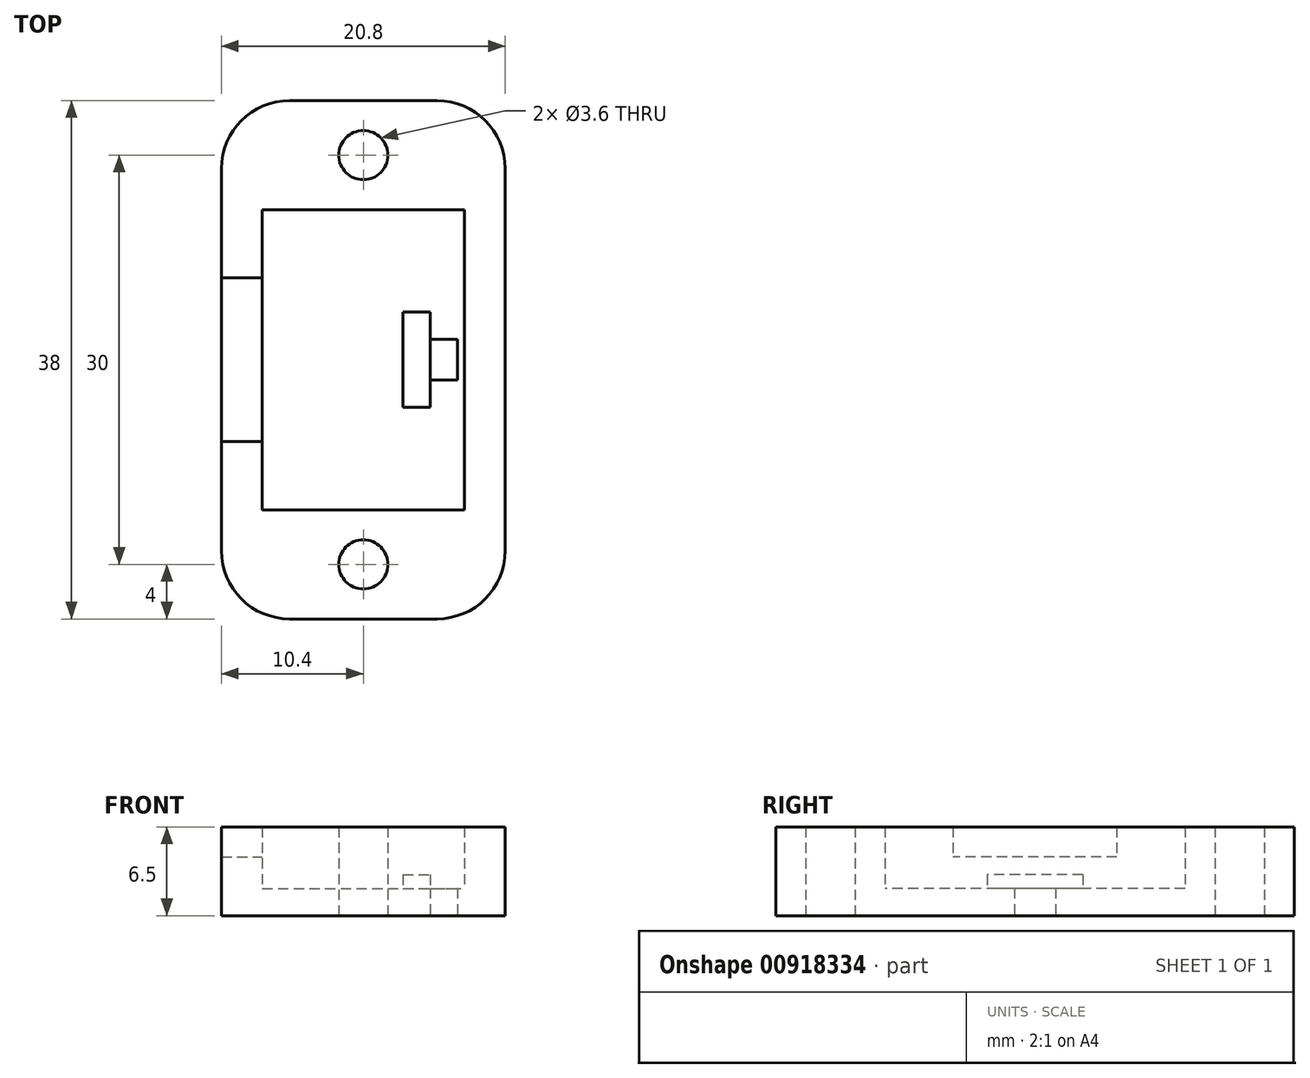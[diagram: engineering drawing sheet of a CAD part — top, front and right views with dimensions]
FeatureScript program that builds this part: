
annotation { "Feature Type Name" : "Feature", "Feature Type Description" : "" }
export const myFeature = defineFeature(function(context is Context, id is Id, definition is map)
    precondition{}
    {
        {
            var Q0;
            Q0=qCreatedBy(makeId("Top.planeOp"),FACE);
            var sketch = newSketch(context, id + "F0", { "sketchPlane" : qUnion([Q0])});
            skLineSegment(sketch, "E0.bottom", {"start": v(-7.4, 11) * mm, "end": v(7.4, 11) * mm});
            skLineSegment(sketch, "E0.top", {"start": v(-7.4, -11) * mm, "end": v(7.4, -11) * mm});
            skLineSegment(sketch, "E0.left", {"start": v(-7.4, 11) * mm, "end": v(-7.4, -11) * mm});
            skLineSegment(sketch, "E0.right", {"start": v(7.4, 11) * mm, "end": v(7.4, -11) * mm});
            skPoint(sketch, "E0.middle", {"position": v(0, 0) * mm});
            skLineSegment(sketch, "E1", {"start": v(2.9, 11) * mm, "end": v(2.9, -11) * mm, "construction": true});
            skLineSegment(sketch, "E2.bottom", {"start": v(2.9, 3.5) * mm, "end": v(4.9, 3.5) * mm});
            skLineSegment(sketch, "E2.top", {"start": v(2.9, -3.5) * mm, "end": v(4.9, -3.5) * mm});
            skLineSegment(sketch, "E2.left", {"start": v(2.9, 3.5) * mm, "end": v(2.9, -3.5) * mm});
            skLineSegment(sketch, "E2.right", {"start": v(4.9, 3.5) * mm, "end": v(4.9, -3.5) * mm});
            skPoint(sketch, "E2.middle", {"position": v(3.9, 0) * mm});
            skLineSegment(sketch, "E3.bottom", {"start": v(-10.4, 19) * mm, "end": v(10.4, 19) * mm});
            skLineSegment(sketch, "E3.top", {"start": v(-10.4, -19) * mm, "end": v(10.4, -19) * mm});
            skLineSegment(sketch, "E3.left", {"start": v(-10.4, 19) * mm, "end": v(-10.4, -19) * mm});
            skLineSegment(sketch, "E3.right", {"start": v(10.4, 19) * mm, "end": v(10.4, -19) * mm});
            skLineSegment(sketch, "E4.bottom", {"start": v(-10.4, 6) * mm, "end": v(-7.4, 6) * mm});
            skLineSegment(sketch, "E4.top", {"start": v(-10.4, -6) * mm, "end": v(-7.4, -6) * mm});
            skLineSegment(sketch, "E4.left", {"start": v(-10.4, 6) * mm, "end": v(-10.4, -6) * mm});
            skLineSegment(sketch, "E4.right", {"start": v(-7.4, 6) * mm, "end": v(-7.4, -6) * mm});
            skPoint(sketch, "E4.middle", {"position": v(-8.9, 0) * mm});
            skCircle(sketch, "E5", {"center": v(0, 15) * mm, "radius": 1.8 * mm});
            skCircle(sketch, "E6", {"center": v(0, -15) * mm, "radius": 1.8 * mm});
            skLineSegment(sketch, "E7.bottom", {"start": v(4.9, 1.5) * mm, "end": v(6.9, 1.5) * mm});
            skLineSegment(sketch, "E7.top", {"start": v(4.9, -1.5) * mm, "end": v(6.9, -1.5) * mm});
            skLineSegment(sketch, "E7.left", {"start": v(4.9, 1.5) * mm, "end": v(4.9, -1.5) * mm});
            skLineSegment(sketch, "E7.right", {"start": v(6.9, 1.5) * mm, "end": v(6.9, -1.5) * mm});
            skPoint(sketch, "E7.middle", {"position": v(5.9, 0) * mm});
            skSolve(sketch);
        }
        {
            var Q0;
            Q0=makeQuery(id+"F0.imprint","IMPRINT",FACE,{"disambiguationData":[TD([[makeQuery(id+"F0.imprint","IMPRINT",EDGE,{"derivedFrom":sQuery(id+"F0.wireOp",EDGE,"E0.bottom")}),1.0]])]});
            extrude(context, id + "F1", {"entities" : qUnion([Q0]), "depth" : 6.5 * mm, "offsetDistance" : 25 * mm});
        }
        {
            var Q0;
            Q0=makeQuery(id+"F0.imprint","IMPRINT",FACE,{"disambiguationData":[TD([[makeQuery(id+"F0.imprint","IMPRINT",EDGE,{"derivedFrom":sQuery(id+"F0.wireOp",EDGE,"E0.bottom")}),-1.0]])]});
            extrude(context, id + "F2", {"entities" : qUnion([Q0]), "operationType" : NewBodyOperationType.ADD, "depth" : 2 * mm, "offsetDistance" : 25 * mm});
        }
        {
            var Q0;
            Q0=makeQuery(id+"F0.imprint","IMPRINT",FACE,{"disambiguationData":[TD([[makeQuery(id+"F0.imprint","IMPRINT",EDGE,{"derivedFrom":sQuery(id+"F0.wireOp",EDGE,"E2.bottom")}),-1.0]])]});
            extrude(context, id + "F3", {"entities" : qUnion([Q0]), "operationType" : NewBodyOperationType.ADD, "depth" : 3 * mm, "offsetDistance" : 25 * mm});
        }
        {
            var Q0;
            Q0=makeQuery(id+"F0.imprint","IMPRINT",FACE,{"disambiguationData":[TD([[makeQuery(id+"F0.imprint","IMPRINT",EDGE,{"derivedFrom":sQuery(id+"F0.wireOp",EDGE,"E4.bottom")}),-1.0]])]});
            extrude(context, id + "F4", {"entities" : qUnion([Q0]), "operationType" : NewBodyOperationType.ADD, "depth" : 4.3 * mm, "offsetDistance" : 25 * mm});
        }
        {
            var Q0;
            Q0=makeQuery(id+"F1.opExtrude","SWEPT_EDGE",EDGE,{"disambiguationData":[OSD([sQuery(id+"F0.wireOp",EDGE,"E3.bottom"),sQuery(id+"F0.wireOp",EDGE,"E3.left")])]});
            var Q1;
            Q1=makeQuery(id+"F1.opExtrude","SWEPT_EDGE",EDGE,{"disambiguationData":[OSD([sQuery(id+"F0.wireOp",EDGE,"E3.bottom"),sQuery(id+"F0.wireOp",EDGE,"E3.right")])]});
            var Q2;
            Q2=makeQuery(id+"F1.opExtrude","SWEPT_EDGE",EDGE,{"disambiguationData":[OSD([sQuery(id+"F0.wireOp",EDGE,"E3.top"),sQuery(id+"F0.wireOp",EDGE,"E3.left")])]});
            var Q3;
            Q3=makeQuery(id+"F1.opExtrude","SWEPT_EDGE",EDGE,{"disambiguationData":[OSD([sQuery(id+"F0.wireOp",EDGE,"E3.top"),sQuery(id+"F0.wireOp",EDGE,"E3.right")])]});
            fillet(context, id + "F5", {"entities" : qUnion([Q0, Q1, Q2, Q3]), "radius" : 5 * mm, "tangentPropagation" : true, "allowEdgeOverflow" : false});
        }
    });
